# Revit family: Konsole 45- 45 Platte längs, fvz.L420
name_source: partatom
category: HLS-Bauteile
revit_build: Autodesk Revit 2018 (Build: 20190510_1515(x64)
units: mm (PartAtom-declared; Revit-internal decimal feet)

## family parameters
Basisbauteil = Fläche
Beim Laden mit Abzugskörper schneiden = Nein
Bemaßung runder Anschluss = Durchmesser verwenden
Gemeinsam genutzt = Ja
Raumberechnungspunkt = Nein
Teiletyp = Normal

## types (1)
- Konsole 45- 45 L= 420 Platte längs fvz
    Artikelnummer = 180450420/fvz
    Ausrichtung Platte = längs
    Breite Platte = 50 mm  [stored 0.164042 ft]
    Breite Profil = 45 mm  [stored 0.147638 ft]
    EAN = 4250928456366
    Fabrikat = MEFA
    Firma = MEFA Befestigungs- und Montagesysteme GmbH
    Gewicht = 1.52 kg
    Gewicht pro Bauteil = 1.52 kg
    Höhe Profil = 45 mm  [stored 0.147638 ft]
    Kurztext1 = Konsole C-Profil 45/45
    Kurztext2 = L= 420 mm Platte längs fsv
    Langloch Platte = 14x20 mm
    Lochabstand = 85 mm
    Lochdurchmesser = 14 mm
    Länge Konsole = 420 mm  [stored 1.37795 ft]
    Länge Platte = 127 mm
    Material = Stahl
    Materialname C-Profil = S235JR
    Materialname Platte = S235JR2
    Oberflaeche = feuerstückverzinkt
    Profil = C-Profil
    Schienenlänge = Montageschiene 45- 45-2,0 für Konsole : C-Profil 45- 45-2,0 L= 420
    Stärke Platte = 8 mm  [stored 0.0262467 ft]
    Stärke Profil = 2 mm  [stored 0.00656168 ft]
    Vorgabe-Ansicht = 1219 mm
    max. zul. Last F1 = 0.56 kip
    max. zul. Last F2 = 0.28 kip
    max. zul. Last q0 = 0.406 kip/ft

note: [stored X ft] marks values corroborated as IEEE doubles in the binary element streams (Revit-internal decimal feet)
